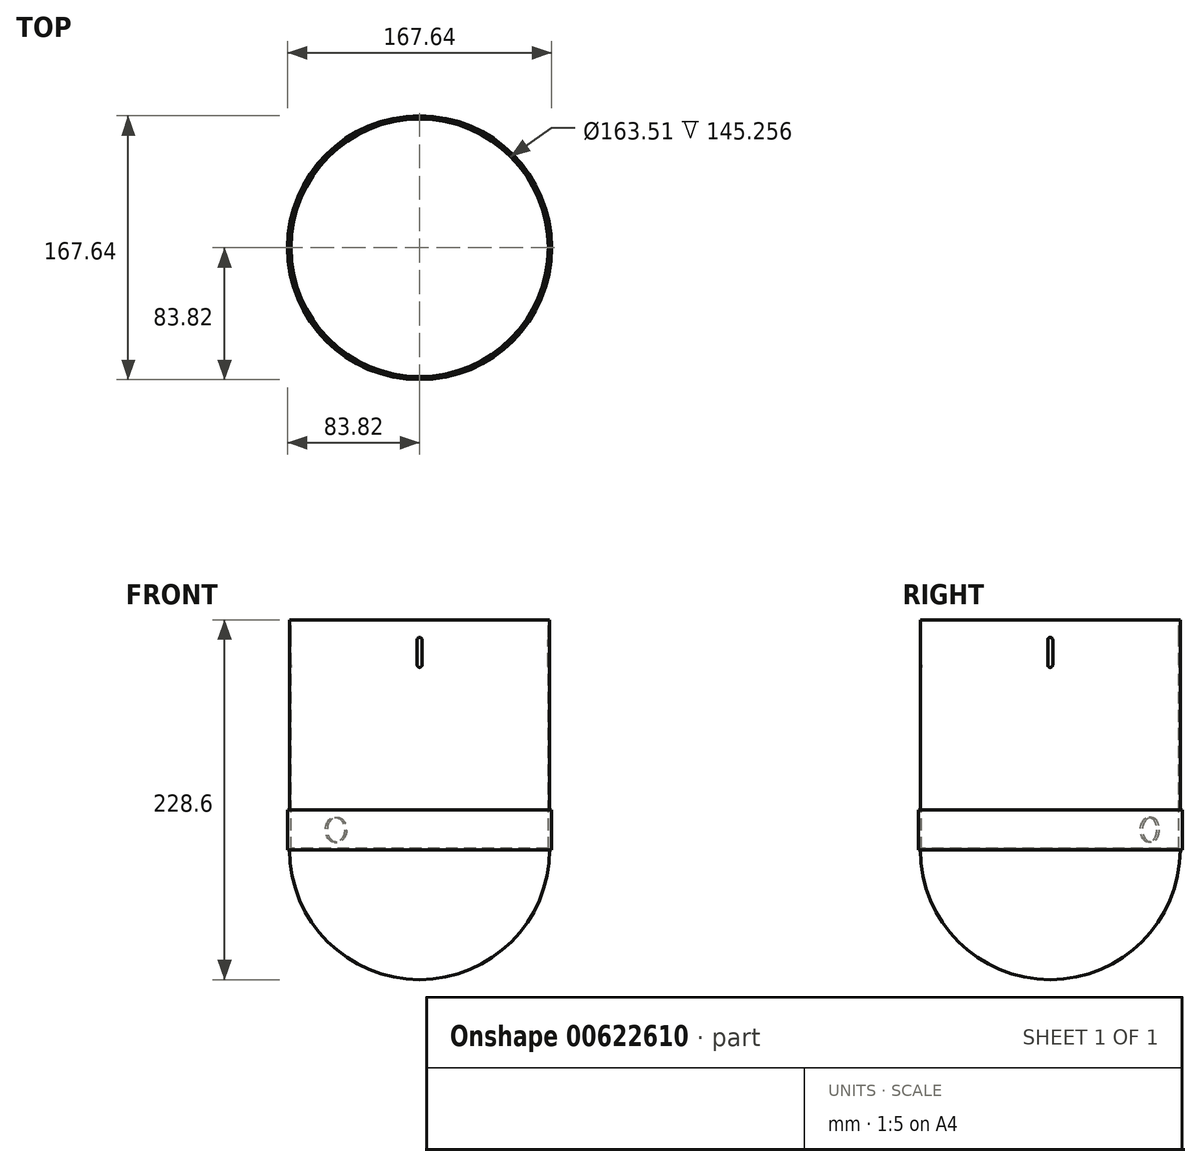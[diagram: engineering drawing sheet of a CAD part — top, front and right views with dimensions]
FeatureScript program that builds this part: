
annotation { "Feature Type Name" : "Feature", "Feature Type Description" : "" }
export const myFeature = defineFeature(function(context is Context, id is Id, definition is map)
    precondition{}
    {
        {
            var Q0;
            Q0=qCreatedBy(makeId("Top.planeOp"),FACE);
            var sketch = newSketch(context, id + "F0", { "sketchPlane" : qUnion([Q0])});
            skCircle(sketch, "E0", {"center": v(0, 0) * mm, "radius": 82.55 * mm});
            skSolve(sketch);
        }
        {
            var Q0;
            Q0=qSketchRegion(id+"F0",true);
            extrude(context, id + "F1", {"entities" : qUnion([Q0]), "oppositeDirection" : true, "depth" : 146.05 * mm, "offsetDistance" : 25.4 * mm});
        }
        {
            var Q0;
            Q0=makeQuery(id+"F1.opExtrude","CAP_FACE",FACE,{"disambiguationData":[OSD([sQuery(id+"F0.wireOp",EDGE,"E0")])],"isStart":true});
            shell(context, id + "F2", {"entities" : qUnion([Q0]), "thickness" : 0.8 * mm});
        }
        {
            var Q0;
            Q0=makeQuery(id+"F1.opExtrude","CAP_EDGE",EDGE,{"disambiguationData":[OSD([sQuery(id+"F0.wireOp",EDGE,"E0")])],"isStart":true});
            cPlane(context, id + "F3", {"entities" : qUnion([Q0]), "cplaneType" : CPlaneType.LINE_ANGLE, "offset" : 165.1 * mm, "angle" : 0 * degree, "width" : 152.4 * mm, "height" : 152.4 * mm});
        }
        {
            var Q0;
            Q0=qCreatedBy(id+"F3.planeOp",FACE);
            var sketch = newSketch(context, id + "F4", { "sketchPlane" : qUnion([Q0])});
            skLineSegment(sketch, "E1", {"start": v(0, 0) * mm, "end": v(32.57, 0) * mm, "construction": true});
            skLineSegment(sketch, "E2", {"start": v(0, 0) * mm, "end": v(-32.1, 0) * mm, "construction": true});
            skLineSegment(sketch, "E3", {"start": v(0, 0) * mm, "end": v(0, -28.58) * mm, "construction": true});
            skLineSegment(sketch, "E4.bottom", {"start": v(-1.59, -28.58) * mm, "end": v(1.59, -28.58) * mm});
            skLineSegment(sketch, "E4.top", {"start": v(-1.59, -12.7) * mm, "end": v(1.59, -12.7) * mm});
            skLineSegment(sketch, "E4.left", {"start": v(-1.59, -28.57) * mm, "end": v(-1.59, -12.7) * mm});
            skLineSegment(sketch, "E4.right", {"start": v(1.59, -28.57) * mm, "end": v(1.59, -12.7) * mm});
            skPoint(sketch, "E4.middle", {"position": v(0, -20.64) * mm});
            skArc(sketch, "E5", {"start": v(1.59, -12.7) * mm, "mid": v(0, -11.11) * mm, "end": v(-1.59, -12.7) * mm});
            skArc(sketch, "E6", {"start": v(-1.59, -28.57) * mm, "mid": v(0, -30.16) * mm, "end": v(1.59, -28.57) * mm});
            skSolve(sketch);
        }
        {
            var Q0;
            Q0=qSketchRegion(id+"F4",true);
            extrude(context, id + "F5", {"entities" : qUnion([Q0]), "operationType" : NewBodyOperationType.REMOVE, "endBound" : BoundingType.SYMMETRIC, "oppositeDirection" : true, "depth" : 177.8 * mm, "offsetDistance" : 25.4 * mm});
        }
        {
            var Q0;
            Q0=makeQuery(id+"F1.opExtrude","CAP_EDGE",EDGE,{"disambiguationData":[OSD([sQuery(id+"F0.wireOp",EDGE,"E0")])],"isStart":true});
            cPlane(context, id + "F6", {"entities" : qUnion([Q0]), "cplaneType" : CPlaneType.LINE_ANGLE, "offset" : 25.4 * mm, "angle" : 90 * degree, "width" : 152.4 * mm, "height" : 152.4 * mm});
        }
        {
            var Q0;
            Q0=qCreatedBy(id+"F6.planeOp",FACE);
            var sketch = newSketch(context, id + "F7", { "sketchPlane" : qUnion([Q0])});
            skLineSegment(sketch, "E7", {"start": v(71.83, 0) * mm, "end": v(-77.17, 0) * mm, "construction": true});
            skLineSegment(sketch, "E8", {"start": v(0, 0) * mm, "end": v(0, -95.04) * mm, "construction": true});
            skLineSegment(sketch, "E9.bottom", {"start": v(1.59, -28.58) * mm, "end": v(-1.59, -28.58) * mm});
            skLineSegment(sketch, "E9.top", {"start": v(1.59, -12.7) * mm, "end": v(-1.59, -12.7) * mm});
            skLineSegment(sketch, "E9.left", {"start": v(1.59, -28.58) * mm, "end": v(1.59, -12.7) * mm});
            skLineSegment(sketch, "E9.right", {"start": v(-1.59, -28.58) * mm, "end": v(-1.59, -12.7) * mm});
            skPoint(sketch, "E9.middle", {"position": v(0, -20.64) * mm});
            skArc(sketch, "E10", {"start": v(1.59, -12.7) * mm, "mid": v(0, -11.11) * mm, "end": v(-1.59, -12.7) * mm});
            skArc(sketch, "E11", {"start": v(-1.59, -28.58) * mm, "mid": v(0, -30.16) * mm, "end": v(1.59, -28.58) * mm});
            skSolve(sketch);
        }
        {
            var Q0;
            Q0=qSketchRegion(id+"F7",true);
            extrude(context, id + "F8", {"entities" : qUnion([Q0]), "operationType" : NewBodyOperationType.REMOVE, "endBound" : BoundingType.SYMMETRIC, "oppositeDirection" : true, "depth" : 177.8 * mm, "offsetDistance" : 25.4 * mm});
        }
        {
            var Q0;
            Q0=makeQuery(id+"F1.opExtrude","CAP_FACE",FACE,{"disambiguationData":[OSD([sQuery(id+"F0.wireOp",EDGE,"E0")])],"isStart":false});
            var sketch = newSketch(context, id + "F9", { "sketchPlane" : qUnion([Q0])});
            skCircle(sketch, "E12", {"center": v(0, 0) * mm, "radius": 83.82 * mm});
            skSolve(sketch);
        }
        {
            var Q0;
            Q0=makeQuery(id+"F9.imprint","IMPRINT",FACE,{"disambiguationData":[TD([[makeQuery(id+"F9.imprint","IMPRINT",EDGE,{"derivedFrom":sQuery(id+"F9.wireOp",EDGE,"E12")}),1.0]])]});
            extrude(context, id + "F10", {"entities" : qUnion([Q0]), "oppositeDirection" : true, "depth" : 25.4 * mm, "offsetDistance" : 25.4 * mm});
        }
        {
            var Q0;
            Q0=makeQuery(id+"F1.opExtrude","CAP_FACE",FACE,{"disambiguationData":[OSD([sQuery(id+"F0.wireOp",EDGE,"E0")])],"isStart":false});
            var sketch = newSketch(context, id + "F11", { "sketchPlane" : qUnion([Q0])});
            skLineSegment(sketch, "E13", {"start": v(0, -82.55) * mm, "end": v(0, 82.55) * mm, "construction": true});
            skLineSegment(sketch, "E14", {"start": v(0, 82.55) * mm, "end": v(0, -82.55) * mm});
            skSolve(sketch);
        }
        {
            var Q0;
            Q0=qSketchRegion(id+"F11",true);
            var Q1;
            {var subQ0=sQuery(id+"F11.wireOp",EDGE,"E14");Q1=makeQuery(id+"F11.imprint","IMPRINT",FACE,{"disambiguationData":[TD([[makeQuery(id+"F11.imprint","IMPRINT",EDGE,{"derivedFrom":subQ0}),-1.0]])]});}
            var Q2;
            Q2=sQuery(id+"F11.wireOp",EDGE,"E14");
            revolve(context, id + "F12", {"operationType" : NewBodyOperationType.ADD, "entities" : qUnion([Q0, Q1]), "axis" : qUnion([Q2]), "revolveType" : RevolveType.ONE_DIRECTION, "oppositeDirection" : true, "angle" : 180 * degree});
        }
        {
            var Q0;
            Q0=makeQuery(id+"F10.opExtrude","SWEPT_FACE",FACE,{"disambiguationData":[OSD([sQuery(id+"F9.wireOp",EDGE,"E12")])]});
            cPlane(context, id + "F13", {"entities" : qUnion([Q0]), "cplaneType" : CPlaneType.LINE_ANGLE, "offset" : 25.4 * mm, "angle" : 130 * degree, "oppositeDirection" : true, "width" : 152.4 * mm, "height" : 152.4 * mm});
        }
        {
            var Q0;
            Q0=qCreatedBy(id+"F13.planeOp",FACE);
            var sketch = newSketch(context, id + "F14", { "sketchPlane" : qUnion([Q0])});
            skLineSegment(sketch, "E15", {"start": v(0, 0) * mm, "end": v(0, -186.05) * mm, "construction": true});
            skLineSegment(sketch, "E16", {"start": v(-83.8, -120.64) * mm, "end": v(-83.8, -146.05) * mm, "construction": true});
            skLineSegment(sketch, "E17", {"start": v(-83.8, -133.34) * mm, "end": v(36.36, -133.34) * mm, "construction": true});
            skCircle(sketch, "E18", {"center": v(0, -133.34) * mm, "radius": 7.94 * mm});
            skSolve(sketch);
        }
        {
            var Q0;
            Q0=qSketchRegion(id+"F14",true);
            extrude(context, id + "F15", {"entities" : qUnion([Q0]), "operationType" : NewBodyOperationType.REMOVE, "oppositeDirection" : true, "depth" : 88.9 * mm, "offsetDistance" : 25.4 * mm});
        }
    });
